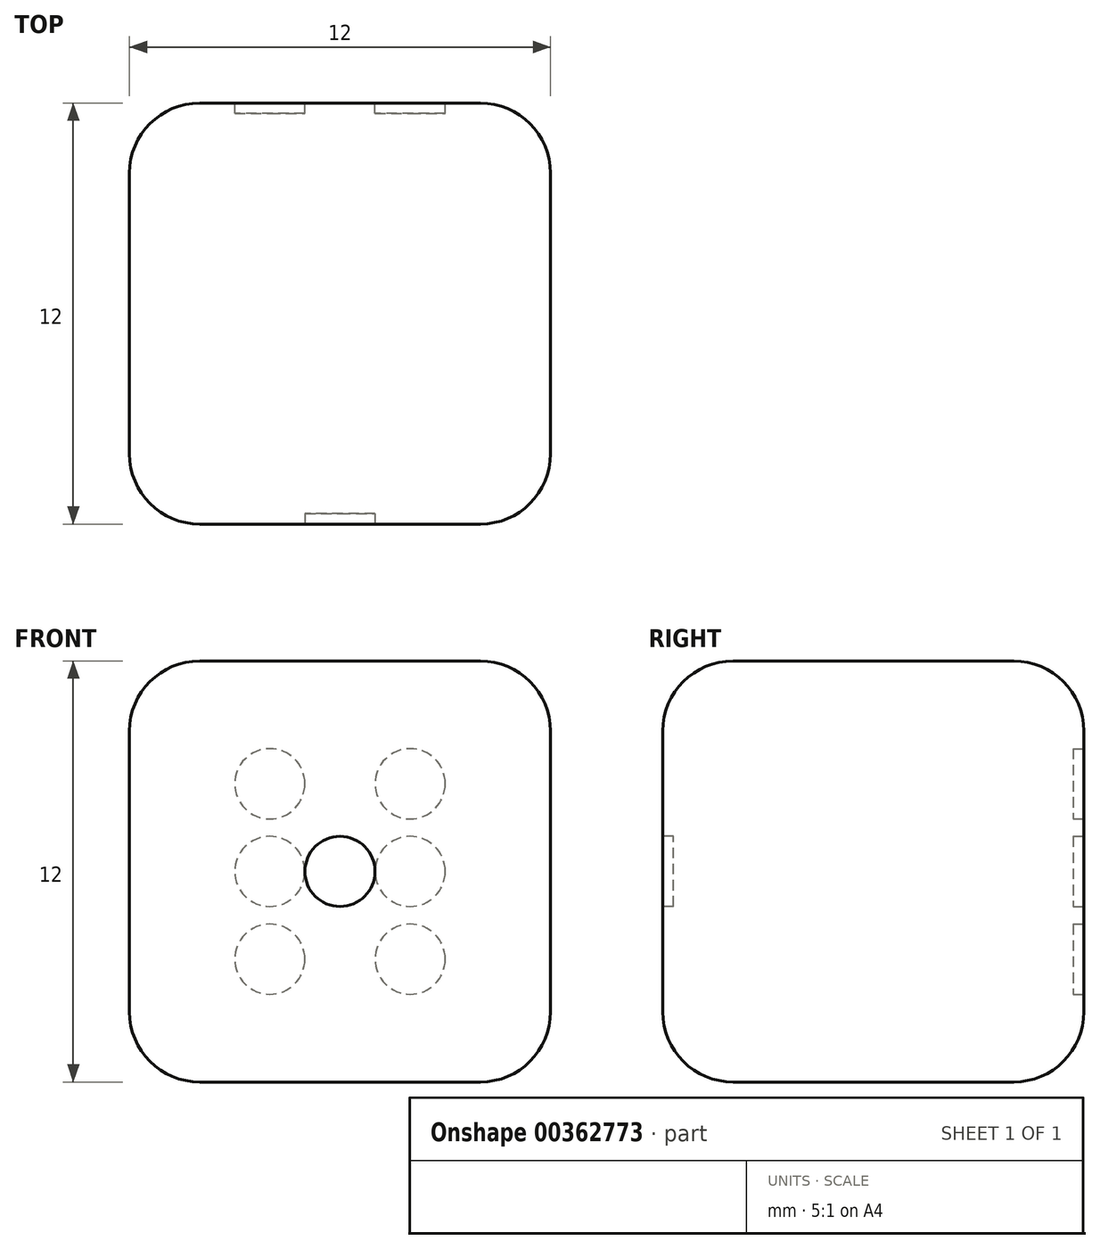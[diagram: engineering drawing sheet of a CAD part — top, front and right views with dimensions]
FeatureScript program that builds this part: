
annotation { "Feature Type Name" : "Feature", "Feature Type Description" : "" }
export const myFeature = defineFeature(function(context is Context, id is Id, definition is map)
    precondition{}
    {
        {
            var Q0;
            Q0=qCreatedBy(makeId("Front.planeOp"),FACE);
            var sketch = newSketch(context, id + "F0", { "sketchPlane" : qUnion([Q0])});
            skLineSegment(sketch, "E0.bottom", {"start": v(-6, 6) * mm, "end": v(6, 6) * mm});
            skLineSegment(sketch, "E0.top", {"start": v(-6, -6) * mm, "end": v(6, -6) * mm});
            skLineSegment(sketch, "E0.left", {"start": v(-6, 6) * mm, "end": v(-6, -6) * mm});
            skLineSegment(sketch, "E0.right", {"start": v(6, 6) * mm, "end": v(6, -6) * mm});
            skSolve(sketch);
        }
        {
            var Q0;
            Q0 = qSketchRegion(id + "F0", true);
            extrude(context, id + "F1", {"entities" : qUnion([Q0]), "depth" : 6 * mm, "hasSecondDirection" : true, "secondDirectionOppositeDirection" : true, "secondDirectionDepth" : 6 * mm});
        }
        {
            var Q0;
            Q0=makeQuery(id+"F1.opExtrude","SWEPT_EDGE",EDGE,{"disambiguationData":[OSD([sQuery(id+"F0.wireOp",EDGE,"E0.top"),sQuery(id+"F0.wireOp",EDGE,"E0.right")])]});
            var Q1;
            Q1=makeQuery(id+"F1.opExtrude","CAP_FACE",FACE,{"disambiguationData":[OSD([sQuery(id+"F0.wireOp",EDGE,"E0.bottom"),sQuery(id+"F0.wireOp",EDGE,"E0.top"),sQuery(id+"F0.wireOp",EDGE,"E0.left"),sQuery(id+"F0.wireOp",EDGE,"E0.right")])],"isStart":true});
            var Q2;
            Q2=makeQuery(id+"F1.opExtrude","SWEPT_EDGE",EDGE,{"disambiguationData":[OSD([sQuery(id+"F0.wireOp",EDGE,"E0.bottom"),sQuery(id+"F0.wireOp",EDGE,"E0.right")])]});
            var Q3;
            Q3=makeQuery(id+"F1.opExtrude","SWEPT_EDGE",EDGE,{"disambiguationData":[OSD([sQuery(id+"F0.wireOp",EDGE,"E0.bottom"),sQuery(id+"F0.wireOp",EDGE,"E0.left")])]});
            var Q4;
            Q4=makeQuery(id+"F1.opExtrude","SWEPT_FACE",FACE,{"disambiguationData":[OSD([sQuery(id+"F0.wireOp",EDGE,"E0.top")])]});
            var Q5;
            Q5=makeQuery(id+"F1.opExtrude","CAP_EDGE",EDGE,{"disambiguationData":[OSD([sQuery(id+"F0.wireOp",EDGE,"E0.bottom")])],"isStart":true});
            var Q6;
            Q6=makeQuery(id+"F1.opExtrude","CAP_EDGE",EDGE,{"disambiguationData":[OSD([sQuery(id+"F0.wireOp",EDGE,"E0.top")])],"isStart":false});
            var Q7;
            Q7=makeQuery(id+"F1.opExtrude","SWEPT_EDGE",EDGE,{"disambiguationData":[OSD([sQuery(id+"F0.wireOp",EDGE,"E0.top"),sQuery(id+"F0.wireOp",EDGE,"E0.left")])]});
            var Q8;
            Q8=makeQuery(id+"F1.opExtrude","SWEPT_FACE",FACE,{"disambiguationData":[OSD([sQuery(id+"F0.wireOp",EDGE,"E0.left")])]});
            var Q9;
            Q9=makeQuery(id+"F1.opExtrude","CAP_EDGE",EDGE,{"disambiguationData":[OSD([sQuery(id+"F0.wireOp",EDGE,"E0.bottom")])],"isStart":false});
            var Q10;
            Q10=makeQuery(id+"F1.opExtrude","CAP_EDGE",EDGE,{"disambiguationData":[OSD([sQuery(id+"F0.wireOp",EDGE,"E0.top")])],"isStart":true});
            var Q11;
            Q11=makeQuery(id+"F1.opExtrude","CAP_EDGE",EDGE,{"disambiguationData":[OSD([sQuery(id+"F0.wireOp",EDGE,"E0.right")])],"isStart":true});
            var Q12;
            Q12=makeQuery(id+"F1.opExtrude","CAP_EDGE",EDGE,{"disambiguationData":[OSD([sQuery(id+"F0.wireOp",EDGE,"E0.right")])],"isStart":false});
            var Q13;
            Q13=makeQuery(id+"F1.opExtrude","CAP_EDGE",EDGE,{"disambiguationData":[OSD([sQuery(id+"F0.wireOp",EDGE,"E0.left")])],"isStart":true});
            var Q14;
            Q14=makeQuery(id+"F1.opExtrude","CAP_EDGE",EDGE,{"disambiguationData":[OSD([sQuery(id+"F0.wireOp",EDGE,"E0.left")])],"isStart":false});
            fillet(context, id + "F2", {"entities" : qUnion([Q0, Q1, Q2, Q3, Q4, Q5, Q6, Q7, Q8, Q9, Q10, Q11, Q12, Q13, Q14]), "radius" : 2 * mm, "tangentPropagation" : true, "allowEdgeOverflow" : false});
        }
        {
            var Q0;
            Q0=makeQuery(id+"F1.opExtrude","CAP_FACE",FACE,{"disambiguationData":[OSD([sQuery(id+"F0.wireOp",EDGE,"E0.bottom"),sQuery(id+"F0.wireOp",EDGE,"E0.top"),sQuery(id+"F0.wireOp",EDGE,"E0.left"),sQuery(id+"F0.wireOp",EDGE,"E0.right")])],"isStart":false});
            var sketch = newSketch(context, id + "F3", { "sketchPlane" : qUnion([Q0])});
            skCircle(sketch, "E1", {"center": v(0, 0) * mm, "radius": 1 * mm});
            skSolve(sketch);
        }
        {
            var Q0;
            Q0 = qSketchRegion(id + "F3", true);
            extrude(context, id + "F4", {"entities" : qUnion([Q0]), "operationType" : NewBodyOperationType.REMOVE, "oppositeDirection" : true, "depth" : 0.3 * mm});
        }
        {
            var Q0;
            Q0=makeQuery(id+"F1.opExtrude","CAP_FACE",FACE,{"disambiguationData":[OSD([sQuery(id+"F0.wireOp",EDGE,"E0.bottom"),sQuery(id+"F0.wireOp",EDGE,"E0.top"),sQuery(id+"F0.wireOp",EDGE,"E0.left"),sQuery(id+"F0.wireOp",EDGE,"E0.right")])],"isStart":true});
            var sketch = newSketch(context, id + "F5", { "sketchPlane" : qUnion([Q0])});
            skCircle(sketch, "E2", {"center": v(-2, 2.5) * mm, "radius": 1 * mm});
            skCircle(sketch, "E3", {"center": v(2, 2.5) * mm, "radius": 1 * mm});
            skCircle(sketch, "E4", {"center": v(2, 0) * mm, "radius": 1 * mm});
            skCircle(sketch, "E5", {"center": v(2, -2.5) * mm, "radius": 1 * mm});
            skCircle(sketch, "E6", {"center": v(-2, 0) * mm, "radius": 1 * mm});
            skCircle(sketch, "E7", {"center": v(-2, -2.5) * mm, "radius": 1 * mm});
            skLineSegment(sketch, "E8", {"start": v(2, 2.5) * mm, "end": v(2, 0) * mm, "construction": true});
            skLineSegment(sketch, "E9", {"start": v(2, -2.5) * mm, "end": v(2, 0) * mm, "construction": true});
            skLineSegment(sketch, "E10", {"start": v(-2, -2.5) * mm, "end": v(-2, 0) * mm, "construction": true});
            skLineSegment(sketch, "E11", {"start": v(-2, 2.5) * mm, "end": v(-2, 0) * mm, "construction": true});
            skLineSegment(sketch, "E12", {"start": v(-2, 2.5) * mm, "end": v(2, 2.5) * mm, "construction": true});
            skSolve(sketch);
        }
        {
            var Q0;
            Q0 = qSketchRegion(id + "F5", true);
            extrude(context, id + "F6", {"entities" : qUnion([Q0]), "operationType" : NewBodyOperationType.REMOVE, "oppositeDirection" : true, "depth" : 0.3 * mm});
        }
    });
